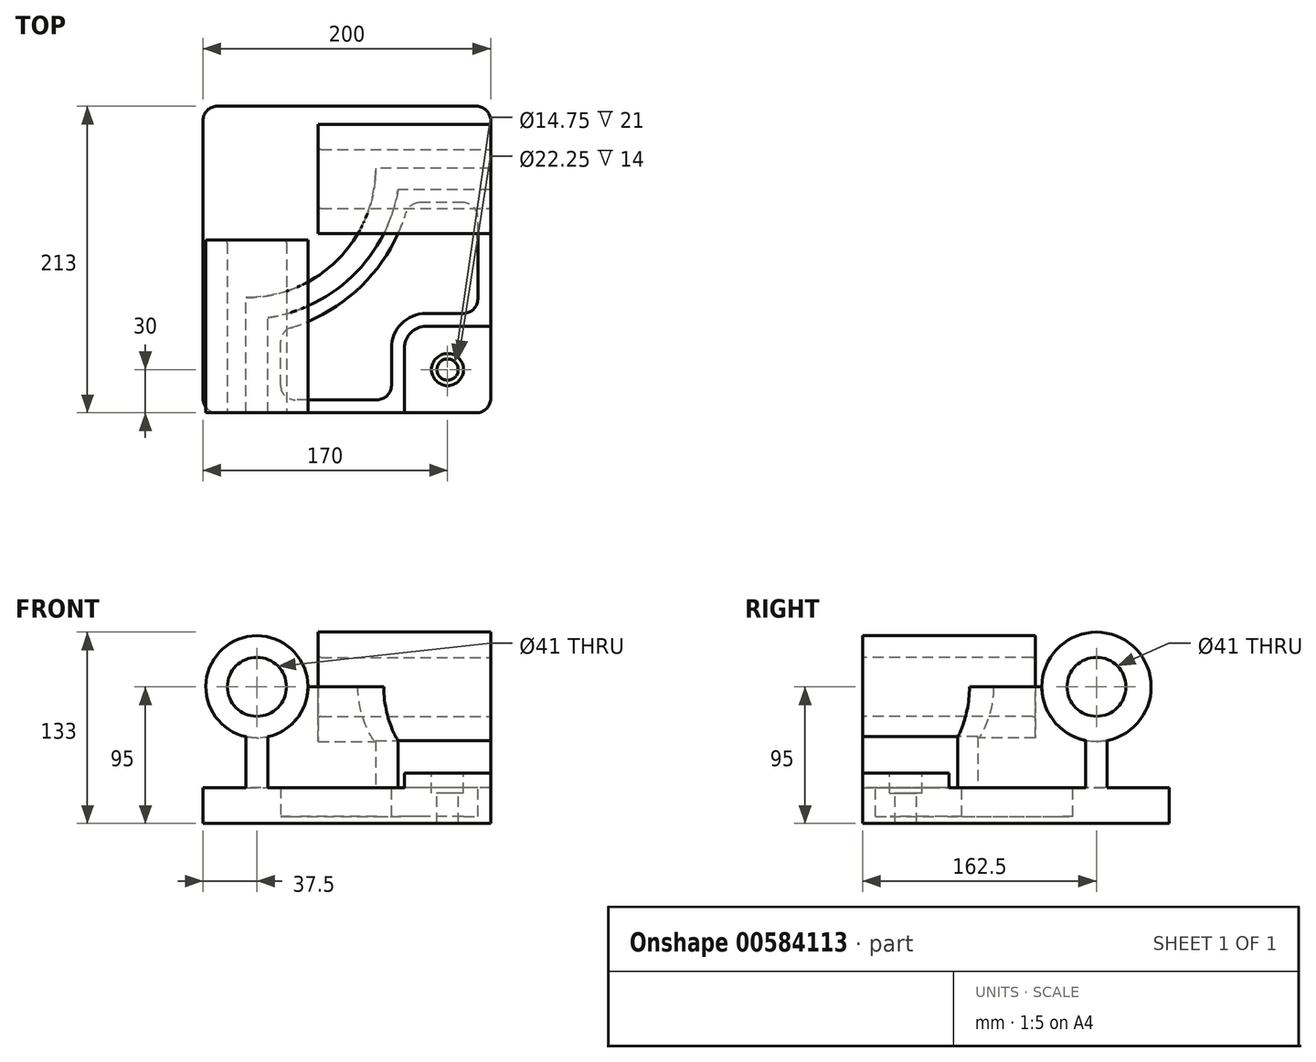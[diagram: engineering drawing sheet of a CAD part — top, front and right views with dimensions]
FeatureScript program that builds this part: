
annotation { "Feature Type Name" : "Feature", "Feature Type Description" : "" }
export const myFeature = defineFeature(function(context is Context, id is Id, definition is map)
    precondition{}
    {
        {
            var Q0;
            Q0=qCreatedBy(makeId("Top.planeOp"),FACE);
            var sketch = newSketch(context, id + "F0", { "sketchPlane" : qUnion([Q0])});
            skLineSegment(sketch, "E0", {"start": v(0, 0) * mm, "end": v(0, 213) * mm});
            skLineSegment(sketch, "E1", {"start": v(0, 213) * mm, "end": v(-200, 213) * mm});
            skLineSegment(sketch, "E2", {"start": v(-200, 213) * mm, "end": v(-200, 0) * mm});
            skLineSegment(sketch, "E3", {"start": v(-200, 0) * mm, "end": v(0, 0) * mm});
            skLineSegment(sketch, "E4", {"start": v(0, 60) * mm, "end": v(-60, 60) * mm});
            skLineSegment(sketch, "E5", {"start": v(-60, 60) * mm, "end": v(-60, 0) * mm});
            skLineSegment(sketch, "E6", {"start": v(-30, 60) * mm, "end": v(-30.25, 0) * mm, "construction": true});
            skLineSegment(sketch, "E7", {"start": v(-60, 30) * mm, "end": v(-30.25, 30) * mm, "construction": true});
            skPoint(sketch, "E8", {"position": v(-30.25, 30) * mm});
            skSolve(sketch);
        }
        {
            var Q0;
            {var subQ3=sQuery(id+"F0.wireOp",EDGE,"E4");Q0=makeQuery(id+"F0.imprint","IMPRINT",FACE,{"disambiguationData":[TD([[makeQuery(id+"F0.imprint","IMPRINT",EDGE,{"derivedFrom":subQ3}),1.0]])]});}
            extrude(context, id + "F1", {"entities" : qUnion([Q0]), "depth" : 35 * mm, "offsetDistance" : 25 * mm});
        }
        {
            var Q0;
            {var subQ3=sQuery(id+"F0.wireOp",EDGE,"E1");Q0=makeQuery(id+"F0.imprint","IMPRINT",FACE,{"disambiguationData":[TD([[makeQuery(id+"F0.imprint","IMPRINT",EDGE,{"derivedFrom":subQ3}),1.0]])]});}
            extrude(context, id + "F2", {"entities" : qUnion([Q0]), "operationType" : NewBodyOperationType.ADD, "depth" : 25 * mm, "offsetDistance" : 25 * mm});
        }
        {
            var Q0;
            Q0=makeQuery(id+"F2.opExtrude","CAP_FACE",FACE,{"disambiguationData":[OSD([sQuery(id+"F0.wireOp",EDGE,"E0"),sQuery(id+"F0.wireOp",EDGE,"E1"),sQuery(id+"F0.wireOp",EDGE,"E2"),sQuery(id+"F0.wireOp",EDGE,"E3"),sQuery(id+"F0.wireOp",EDGE,"E4"),sQuery(id+"F0.wireOp",EDGE,"E5")])],"isStart":false});
            var sketch = newSketch(context, id + "F3", { "sketchPlane" : qUnion([Q0])});
            skLineSegment(sketch, "E9", {"start": v(-60, 0) * mm, "end": v(-69, 0) * mm, "construction": true});
            skLineSegment(sketch, "E10", {"start": v(0, 60) * mm, "end": v(0, 69) * mm, "construction": true});
            skLineSegment(sketch, "E11", {"start": v(-69, 0) * mm, "end": v(-69, 29) * mm, "construction": true});
            skLineSegment(sketch, "E12", {"start": v(-34, 69) * mm, "end": v(0, 69) * mm, "construction": true});
            skSolve(sketch);
        }
        {
            var Q0;
            Q0=makeQuery(id+"F1.opExtrude","SWEPT_EDGE",EDGE,{"disambiguationData":[OSD([sQuery(id+"F0.wireOp",EDGE,"E4"),sQuery(id+"F0.wireOp",EDGE,"E5")])]});
            fillet(context, id + "F4", {"entities" : qUnion([Q0]), "radius" : 15 * mm, "tangentPropagation" : true, "allowEdgeOverflow" : false});
        }
        {
            var Q0;
            Q0=makeQuery(id+"F3.imprint","IMPRINT",FACE,{"disambiguationData":[TD([[makeQuery(id+"F3.imprint","IMPRINT",EDGE,{"derivedFrom":makeQuery(id+"F2.opExtrude","CAP_EDGE",EDGE,{"disambiguationData":[OSD([sQuery(id+"F0.wireOp",EDGE,"E0")])],"isStart":false})}),1.0]])]});
            var sketch = newSketch(context, id + "F5", { "sketchPlane" : qUnion([Q0])});
            skLineSegment(sketch, "E13.0", {"start": v(-69, 45) * mm, "end": v(-69, 9) * mm});
            skArc(sketch, "E13.1", {"start": v(-45, 69) * mm, "mid": v(-61.97, 61.97) * mm, "end": v(-69, 45) * mm});
            skLineSegment(sketch, "E13.2", {"start": v(-9, 69) * mm, "end": v(-45, 69) * mm});
            skLineSegment(sketch, "E14", {"start": v(-69, 9) * mm, "end": v(-146, 9) * mm});
            skLineSegment(sketch, "E15", {"start": v(-9, 69) * mm, "end": v(-9, 146) * mm});
            skLineSegment(sketch, "E16", {"start": v(-9, 146) * mm, "end": v(-56.93, 146) * mm});
            skLineSegment(sketch, "E17", {"start": v(-146, 9) * mm, "end": v(-146, 57.06) * mm});
            skLineSegment(sketch, "E18", {"start": v(-155, 0) * mm, "end": v(-155, 65.98) * mm});
            skLineSegment(sketch, "E19", {"start": v(-170, 0) * mm, "end": v(-170, 80) * mm});
            skLineSegment(sketch, "E20", {"start": v(0, 155) * mm, "end": v(-64.3, 155) * mm});
            skLineSegment(sketch, "E21", {"start": v(0, 170) * mm, "end": v(-80, 170) * mm});
            skArc(sketch, "E22", {"start": v(-170, 80) * mm, "mid": v(-106.36, 106.36) * mm, "end": v(-80, 170) * mm});
            skArc(sketch, "E23", {"start": v(-155, 65.98) * mm, "mid": v(-95.27, 95.84) * mm, "end": v(-64.3, 155) * mm});
            skArc(sketch, "E24", {"start": v(-146, 57.06) * mm, "mid": v(-88.98, 89.03) * mm, "end": v(-56.93, 146) * mm});
            skSolve(sketch);
        }
        {
            var Q0;
            Q0=makeQuery(id+"F5.imprint","IMPRINT",FACE,{"disambiguationData":[TD([[makeQuery(id+"F5.imprint","IMPRINT",EDGE,{"derivedFrom":sQuery(id+"F5.wireOp",EDGE,"E13.0")}),-1.0]])]});
            extrude(context, id + "F6", {"entities" : qUnion([Q0]), "operationType" : NewBodyOperationType.REMOVE, "oppositeDirection" : true, "depth" : 20 * mm, "offsetDistance" : 25 * mm});
        }
        {
            var Q0;
            {var subQ4=sQuery(id+"F5.wireOp",EDGE,"E18");Q0=makeQuery(id+"F5.imprint","IMPRINT",FACE,{"disambiguationData":[TD([[makeQuery(id+"F5.imprint","IMPRINT",EDGE,{"derivedFrom":subQ4}),1.0]])]});}
            extrude(context, id + "F7", {"entities" : qUnion([Q0]), "operationType" : NewBodyOperationType.ADD, "depth" : 70 * mm, "offsetDistance" : 25 * mm});
        }
        {
            var Q0;
            Q0=makeQuery(id+"F6.boolean.opBoolean","COPY",EDGE,{"derivedFrom":makeQuery(id+"F6.opExtrude","SWEPT_EDGE",EDGE,{"disambiguationData":[OSD([sQuery(id+"F5.wireOp",EDGE,"E14"),sQuery(id+"F5.wireOp",EDGE,"E17")])]})});
            var Q1;
            Q1=makeQuery(id+"F6.boolean.opBoolean","COPY",EDGE,{"derivedFrom":makeQuery(id+"F6.opExtrude","SWEPT_EDGE",EDGE,{"disambiguationData":[OSD([sQuery(id+"F5.wireOp",EDGE,"E17"),sQuery(id+"F5.wireOp",EDGE,"KFK1ySTx-jrWD-zjO2-nNrS-KvNsCisoXZ95")])]})});
            var Q2;
            Q2=makeQuery(id+"F6.boolean.opBoolean","COPY",EDGE,{"derivedFrom":makeQuery(id+"F6.opExtrude","SWEPT_EDGE",EDGE,{"disambiguationData":[OSD([sQuery(id+"F5.wireOp",EDGE,"E16"),sQuery(id+"F5.wireOp",EDGE,"KFK1ySTx-jrWD-zjO2-nNrS-KvNsCisoXZ95")])]})});
            var Q3;
            Q3=makeQuery(id+"F6.boolean.opBoolean","COPY",EDGE,{"derivedFrom":makeQuery(id+"F6.opExtrude","SWEPT_EDGE",EDGE,{"disambiguationData":[OSD([sQuery(id+"F5.wireOp",EDGE,"E15"),sQuery(id+"F5.wireOp",EDGE,"E16")])]})});
            var Q4;
            Q4=makeQuery(id+"F6.boolean.opBoolean","COPY",EDGE,{"derivedFrom":makeQuery(id+"F6.opExtrude","SWEPT_EDGE",EDGE,{"disambiguationData":[OSD([sQuery(id+"F5.wireOp",EDGE,"E13.2"),sQuery(id+"F5.wireOp",EDGE,"E15")])]})});
            var Q5;
            Q5=makeQuery(id+"F6.boolean.opBoolean","COPY",EDGE,{"derivedFrom":makeQuery(id+"F6.opExtrude","SWEPT_EDGE",EDGE,{"disambiguationData":[OSD([sQuery(id+"F5.wireOp",EDGE,"E13.0"),sQuery(id+"F5.wireOp",EDGE,"E14")])]})});
            fillet(context, id + "F8", {"entities" : qUnion([Q0, Q1, Q2, Q3, Q4, Q5]), "radius" : 10 * mm, "tangentPropagation" : true, "allowEdgeOverflow" : false});
        }
        {
            var Q0;
            Q0=makeQuery(id+"F1.opExtrude","CAP_FACE",FACE,{"disambiguationData":[OSD([sQuery(id+"F0.wireOp",EDGE,"E0"),sQuery(id+"F0.wireOp",EDGE,"E3"),sQuery(id+"F0.wireOp",EDGE,"E4"),sQuery(id+"F0.wireOp",EDGE,"E5")])],"isStart":false});
            var sketch = newSketch(context, id + "F9", { "sketchPlane" : qUnion([Q0])});
            skLineSegment(sketch, "E25", {"start": v(-60, 0) * mm, "end": v(-60, 62.3) * mm, "construction": true});
            skLineSegment(sketch, "E26", {"start": v(-60, 62.3) * mm, "end": v(-60, 60) * mm, "construction": true});
            skLineSegment(sketch, "E27", {"start": v(-60, 60) * mm, "end": v(0, 60) * mm, "construction": true});
            skLineSegment(sketch, "E28", {"start": v(-30, 60) * mm, "end": v(-30, 0) * mm, "construction": true});
            skPoint(sketch, "E29", {"position": v(-30, 30) * mm});
            skSolve(sketch);
        }
        {
            var Q0;
            Q0=sQuery(id+"F9.wireOp",VERTEX,"E29");
            var Q1;
            Q1=makeQuery(id+"F1.opExtrude","SWEPT_BODY",BODY,{"disambiguationData":[OSD([sQuery(id+"F0.wireOp",EDGE,"E0"),sQuery(id+"F0.wireOp",EDGE,"E3"),sQuery(id+"F0.wireOp",EDGE,"E4"),sQuery(id+"F0.wireOp",EDGE,"E5")])]});
            hole(context, id + "F10", {"style" : HoleStyle.C_BORE, "endStyle" : HoleEndStyle.THROUGH, "standardTappedOrClearance" : lookupTablePath({ "standard" : "ISO", "fit" : "Close", "size" : "M14", "type" : "Clearance" }), "standardBlindInLast" : lookupTablePath({ "fit" : "Close", "standard" : "ISO", "size" : "M14", "type" : "Clearance" }), "holeDiameter" : 14.75 * mm, "cBoreDiameter" : 22.25 * mm, "cBoreDepth" : 14 * mm, "majorDiameter" : 5 * mm, "isTappedThrough" : true, "tappedDepth" : 12 * mm, "tapClearance" : 3, "locations" : qUnion([Q0]), "scope" : qUnion([Q1])});
        }
        {
            var Q0;
            {var subQ0=sQuery(id+"F0.wireOp",EDGE,"E3");Q0=makeQuery(id+"F7.boolean.opBoolean","MERGE",FACE,{"derivedFrom":[makeQuery(id+"F2.boolean.opBoolean","MERGE",FACE,{"derivedFrom":[makeQuery(id+"F1.opExtrude","SWEPT_FACE",FACE,{"disambiguationData":[OSD([subQ0])]}),makeQuery(id+"F2.opExtrude","SWEPT_FACE",FACE,{"disambiguationData":[OSD([subQ0])]})]}),makeQuery(id+"F7.opExtrude","SWEPT_FACE",FACE,{"disambiguationData":[OSD([subQ0])]})]});}
            var sketch = newSketch(context, id + "F11", { "sketchPlane" : qUnion([Q0])});
            skLineSegment(sketch, "E30", {"start": v(-170, 81.46) * mm, "end": v(-155, 81.46) * mm, "construction": true});
            skLineSegment(sketch, "E31", {"start": v(-162.5, 81.46) * mm, "end": v(-162.5, 0) * mm, "construction": true});
            skLineSegment(sketch, "E32", {"start": v(-162.5, 0) * mm, "end": v(-162.5, 95) * mm, "construction": true});
            skCircle(sketch, "E33", {"center": v(-162.5, 95) * mm, "radius": 35.5 * mm});
            skCircle(sketch, "E34", {"center": v(-162.5, 95) * mm, "radius": 20.5 * mm});
            skSolve(sketch);
        }
        {
            var Q0;
            {var subQ0=sQuery(id+"F11.wireOp",EDGE,"E33");var subQ1=sQuery(id+"F0.wireOp",EDGE,"E3");var subQ2=makeQuery(id+"F7.opExtrude","SWEPT_EDGE",EDGE,{"disambiguationData":[OSD([subQ1,sQuery(id+"F5.wireOp",EDGE,"E18")])]});var subQ3=makeQuery(id+"F11.imprint","INTERSECT",VERTEX,{"derivedFrom":[subQ2,subQ0]});Q0=makeQuery(id+"F11.imprint","IMPRINT",FACE,{"disambiguationData":[TD([[makeQuery(id+"F11.imprint","IMPRINT",EDGE,{"disambiguationData":[TD([[subQ3,-1.0]])],"derivedFrom":subQ0}),1.0]])]});}
            var Q1;
            {var subQ0=sQuery(id+"F11.wireOp",EDGE,"E33");var subQ1=sQuery(id+"F0.wireOp",EDGE,"E3");var subQ2=makeQuery(id+"F7.opExtrude","SWEPT_EDGE",EDGE,{"disambiguationData":[OSD([subQ1,sQuery(id+"F5.wireOp",EDGE,"E18")])]});var subQ3=makeQuery(id+"F11.imprint","INTERSECT",VERTEX,{"derivedFrom":[subQ2,subQ0]});Q1=makeQuery(id+"F11.imprint","IMPRINT",FACE,{"disambiguationData":[TD([[makeQuery(id+"F11.imprint","IMPRINT",EDGE,{"disambiguationData":[TD([[subQ3,1.0]])],"derivedFrom":subQ0}),1.0]])]});}
            extrude(context, id + "F12", {"entities" : qUnion([Q0, Q1]), "operationType" : NewBodyOperationType.ADD, "oppositeDirection" : true, "depth" : 120 * mm, "offsetDistance" : 25 * mm});
        }
        {
            var Q0;
            {var subQ0=sQuery(id+"F0.wireOp",EDGE,"E3");Q0=makeQuery(id+"F12.boolean.opBoolean","MERGE",FACE,{"derivedFrom":[makeQuery(id+"F7.boolean.opBoolean","MERGE",FACE,{"derivedFrom":[makeQuery(id+"F2.boolean.opBoolean","MERGE",FACE,{"derivedFrom":[makeQuery(id+"F1.opExtrude","SWEPT_FACE",FACE,{"disambiguationData":[OSD([subQ0])]}),makeQuery(id+"F2.opExtrude","SWEPT_FACE",FACE,{"disambiguationData":[OSD([subQ0])]})]}),makeQuery(id+"F7.opExtrude","SWEPT_FACE",FACE,{"disambiguationData":[OSD([subQ0])]})]}),makeQuery(id+"F12.opExtrude","CAP_FACE",FACE,{"disambiguationData":[OSD([sQuery(id+"F11.wireOp",EDGE,"E33"),sQuery(id+"F11.wireOp",EDGE,"E34")])],"isStart":true})]});}
            var sketch = newSketch(context, id + "F13", { "sketchPlane" : qUnion([Q0])});
            skPoint(sketch, "E35", {"position": v(-162.5, 95) * mm});
            skSolve(sketch);
        }
        {
            var Q0;
            Q0=sQuery(id+"F13.wireOp",VERTEX,"E35");
            var Q1;
            Q1=makeQuery(id+"F1.opExtrude","SWEPT_BODY",BODY,{"disambiguationData":[OSD([sQuery(id+"F0.wireOp",EDGE,"E0"),sQuery(id+"F0.wireOp",EDGE,"E3"),sQuery(id+"F0.wireOp",EDGE,"E4"),sQuery(id+"F0.wireOp",EDGE,"E5")])]});
            hole(context, id + "F14", {"style" : HoleStyle.SIMPLE, "endStyle" : HoleEndStyle.THROUGH, "holeDiameter" : 41 * mm, "majorDiameter" : 5 * mm, "isTappedThrough" : true, "tappedDepth" : 12 * mm, "tapClearance" : 3, "locations" : qUnion([Q0]), "scope" : qUnion([Q1])});
        }
        {
            var Q0;
            {var subQ0=sQuery(id+"F0.wireOp",EDGE,"E0");Q0=makeQuery(id+"F7.boolean.opBoolean","MERGE",FACE,{"derivedFrom":[makeQuery(id+"F2.boolean.opBoolean","MERGE",FACE,{"derivedFrom":[makeQuery(id+"F1.opExtrude","SWEPT_FACE",FACE,{"disambiguationData":[OSD([subQ0])]}),makeQuery(id+"F2.opExtrude","SWEPT_FACE",FACE,{"disambiguationData":[OSD([subQ0])]})]}),makeQuery(id+"F7.opExtrude","SWEPT_FACE",FACE,{"disambiguationData":[OSD([subQ0])]})]});}
            var sketch = newSketch(context, id + "F15", { "sketchPlane" : qUnion([Q0])});
            skLineSegment(sketch, "E36", {"start": v(155, 37.38) * mm, "end": v(170, 37.38) * mm, "construction": true});
            skLineSegment(sketch, "E37", {"start": v(162.5, 37.38) * mm, "end": v(162.5, 0) * mm, "construction": true});
            skLineSegment(sketch, "E38", {"start": v(162.5, 0) * mm, "end": v(162.5, 95) * mm, "construction": true});
            skCircle(sketch, "E39", {"center": v(162.5, 95) * mm, "radius": 20.5 * mm});
            skCircle(sketch, "E40", {"center": v(162.5, 95) * mm, "radius": 38 * mm});
            skSolve(sketch);
        }
        {
            var Q0;
            {var subQ0=sQuery(id+"F15.wireOp",EDGE,"E39");var subQ1=sQuery(id+"F0.wireOp",EDGE,"E0");var subQ2=makeQuery(id+"F7.opExtrude","SWEPT_EDGE",EDGE,{"disambiguationData":[OSD([subQ1,sQuery(id+"F5.wireOp",EDGE,"E20")])]});var subQ3=makeQuery(id+"F15.imprint","INTERSECT",VERTEX,{"derivedFrom":[subQ2,subQ0]});Q0=makeQuery(id+"F15.imprint","IMPRINT",FACE,{"disambiguationData":[TD([[makeQuery(id+"F15.imprint","IMPRINT",EDGE,{"disambiguationData":[TD([[subQ3,1.0]])],"derivedFrom":subQ0}),-1.0]])]});}
            var Q1;
            {var subQ0=sQuery(id+"F15.wireOp",EDGE,"E39");var subQ1=sQuery(id+"F0.wireOp",EDGE,"E0");var subQ2=makeQuery(id+"F7.opExtrude","SWEPT_EDGE",EDGE,{"disambiguationData":[OSD([subQ1,sQuery(id+"F5.wireOp",EDGE,"E20")])]});var subQ3=makeQuery(id+"F15.imprint","INTERSECT",VERTEX,{"derivedFrom":[subQ2,subQ0]});Q1=makeQuery(id+"F15.imprint","IMPRINT",FACE,{"disambiguationData":[TD([[makeQuery(id+"F15.imprint","IMPRINT",EDGE,{"disambiguationData":[TD([[subQ3,-1.0]])],"derivedFrom":subQ0}),-1.0]])]});}
            extrude(context, id + "F16", {"entities" : qUnion([Q0, Q1]), "operationType" : NewBodyOperationType.ADD, "oppositeDirection" : true, "depth" : 120 * mm, "offsetDistance" : 25 * mm});
        }
        {
            var Q0;
            Q0=sQuery(id+"F15.wireOp",VERTEX,"E39.center");
            var Q1;
            Q1=makeQuery(id+"F1.opExtrude","SWEPT_BODY",BODY,{"disambiguationData":[OSD([sQuery(id+"F0.wireOp",EDGE,"E0"),sQuery(id+"F0.wireOp",EDGE,"E3"),sQuery(id+"F0.wireOp",EDGE,"E4"),sQuery(id+"F0.wireOp",EDGE,"E5")])]});
            hole(context, id + "F17", {"style" : HoleStyle.SIMPLE, "endStyle" : HoleEndStyle.THROUGH, "holeDiameter" : 41 * mm, "majorDiameter" : 5 * mm, "isTappedThrough" : true, "tappedDepth" : 12 * mm, "tapClearance" : 3, "locations" : qUnion([Q0]), "scope" : qUnion([Q1])});
        }
        {
            var Q0;
            Q0=makeQuery(id+"F14.hole-0.boolean.opBoolean","MERGE",EDGE,{"derivedFrom":[makeQuery(id+"F12.opExtrude","CAP_EDGE",EDGE,{"disambiguationData":[OSD([sQuery(id+"F11.wireOp",EDGE,"E34")])],"isStart":true}),makeQuery(id+"F14.hole-0.opRevolve","SWEPT_EDGE",EDGE,{"disambiguationData":[OSD([sQuery(id+"F14.hole-0.sketch.wireOp",EDGE,"core_line_2"),sQuery(id+"F14.hole-0.sketch.wireOp",EDGE,"core_line_3")])]})]});
            var Q1;
            Q1=makeQuery(id+"F17.hole-0.boolean.opBoolean","MERGE",EDGE,{"derivedFrom":[makeQuery(id+"F16.opExtrude","CAP_EDGE",EDGE,{"disambiguationData":[OSD([sQuery(id+"F15.wireOp",EDGE,"E39")])],"isStart":true}),makeQuery(id+"F17.hole-0.opRevolve","SWEPT_EDGE",EDGE,{"disambiguationData":[OSD([sQuery(id+"F17.hole-0.sketch.wireOp",EDGE,"core_line_2"),sQuery(id+"F17.hole-0.sketch.wireOp",EDGE,"core_line_3")])]})]});
            var Q2;
            Q2=makeQuery(id+"F12.opExtrude","CAP_EDGE",EDGE,{"disambiguationData":[OSD([sQuery(id+"F11.wireOp",EDGE,"E34")])],"isStart":false});
            var Q3;
            Q3=makeQuery(id+"F16.opExtrude","CAP_EDGE",EDGE,{"disambiguationData":[OSD([sQuery(id+"F15.wireOp",EDGE,"E39")])],"isStart":false});
            fillet(context, id + "F18", {"entities" : qUnion([Q0, Q1, Q2, Q3]), "radius" : 2 * mm, "tangentPropagation" : true, "allowEdgeOverflow" : false});
        }
        {
            var Q0;
            Q0=makeQuery(id+"F1.opExtrude","SWEPT_EDGE",EDGE,{"disambiguationData":[OSD([sQuery(id+"F0.wireOp",EDGE,"E0"),sQuery(id+"F0.wireOp",EDGE,"E3")])]});
            var Q1;
            Q1=makeQuery(id+"F2.opExtrude","SWEPT_EDGE",EDGE,{"disambiguationData":[OSD([sQuery(id+"F0.wireOp",EDGE,"E0"),sQuery(id+"F0.wireOp",EDGE,"E1")])]});
            var Q2;
            Q2=makeQuery(id+"F2.opExtrude","SWEPT_EDGE",EDGE,{"disambiguationData":[OSD([sQuery(id+"F0.wireOp",EDGE,"E1"),sQuery(id+"F0.wireOp",EDGE,"E2")])]});
            var Q3;
            Q3=makeQuery(id+"F2.opExtrude","SWEPT_EDGE",EDGE,{"disambiguationData":[OSD([sQuery(id+"F0.wireOp",EDGE,"E2"),sQuery(id+"F0.wireOp",EDGE,"E3")])]});
            fillet(context, id + "F19", {"entities" : qUnion([Q0, Q1, Q2, Q3]), "radius" : 10 * mm, "tangentPropagation" : true, "allowEdgeOverflow" : false});
        }
    });
